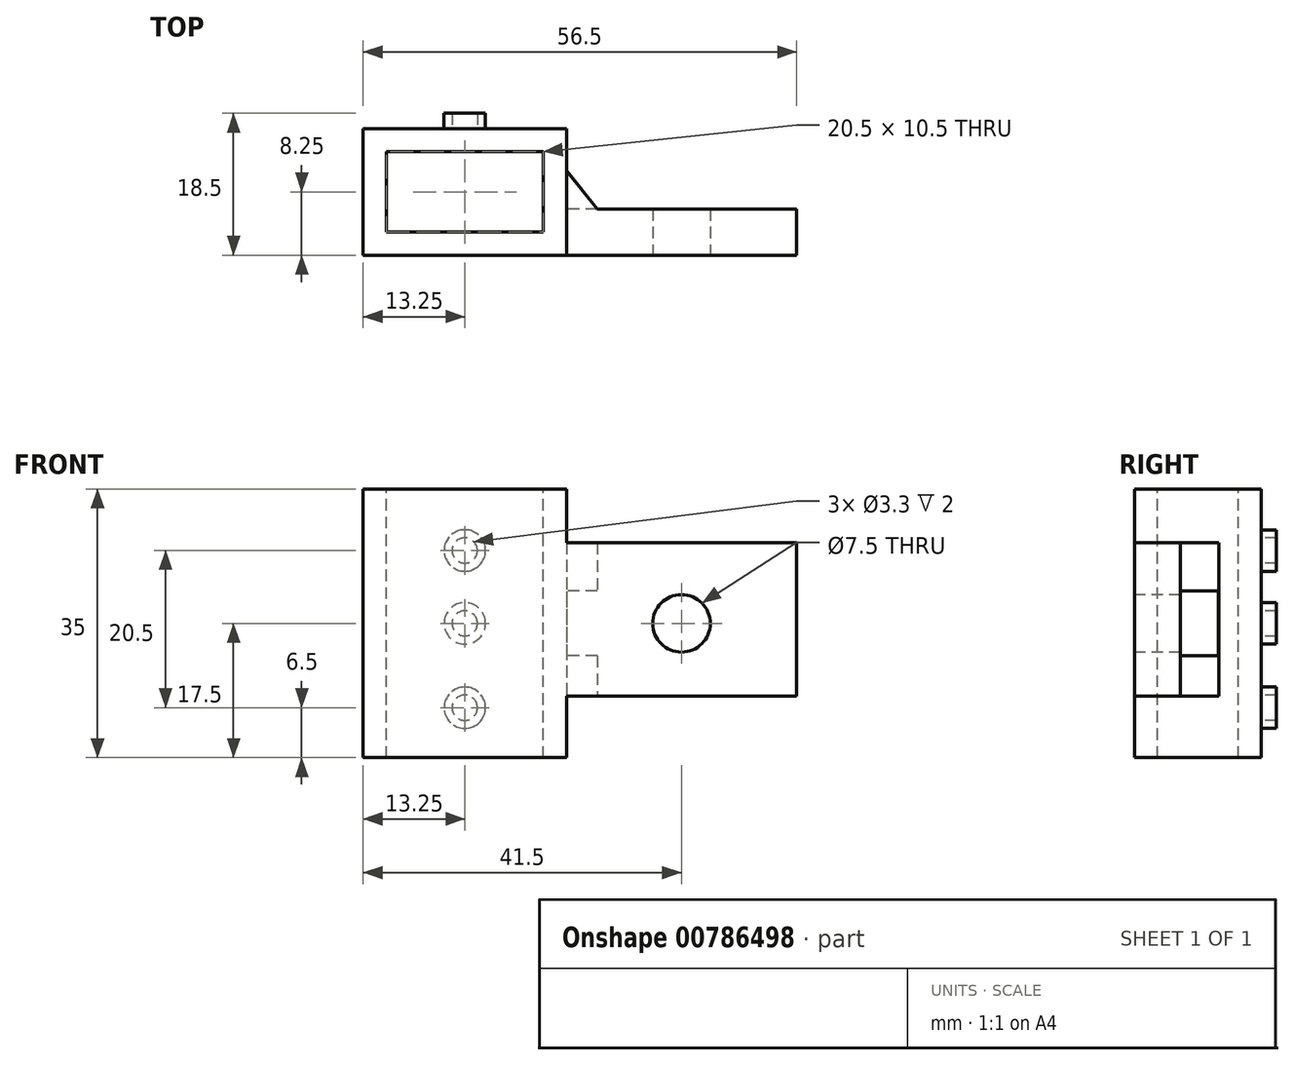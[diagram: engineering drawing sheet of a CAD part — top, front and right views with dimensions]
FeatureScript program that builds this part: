
annotation { "Feature Type Name" : "Feature", "Feature Type Description" : "" }
export const myFeature = defineFeature(function(context is Context, id is Id, definition is map)
    precondition{}
    {
        {
            var Q0;
            Q0=qCreatedBy(makeId("Front.planeOp"),FACE);
            var sketch = newSketch(context, id + "F0", { "sketchPlane" : qUnion([Q0])});
            skLineSegment(sketch, "E0.bottom", {"start": v(-13.25, 17.5) * mm, "end": v(13.25, 17.5) * mm});
            skLineSegment(sketch, "E0.top", {"start": v(-13.25, -17.5) * mm, "end": v(13.25, -17.5) * mm});
            skLineSegment(sketch, "E0.left", {"start": v(-13.25, 17.5) * mm, "end": v(-13.25, -17.5) * mm});
            skLineSegment(sketch, "E0.right", {"start": v(13.25, 17.5) * mm, "end": v(13.25, -17.5) * mm});
            skSolve(sketch);
        }
        {
            var Q0;
            Q0 = qSketchRegion(id + "F0", true);
            extrude(context, id + "F1", {"entities" : qUnion([Q0]), "depth" : 16.5 * mm, "offsetDistance" : 25 * mm});
        }
        {
            var Q0;
            Q0=makeQuery(id+"F1.opExtrude","SWEPT_FACE",FACE,{"disambiguationData":[OSD([sQuery(id+"F0.wireOp",EDGE,"E0.bottom")])]});
            var sketch = newSketch(context, id + "F2", { "sketchPlane" : qUnion([Q0])});
            skLineSegment(sketch, "E1.bottom", {"start": v(-10.25, -3) * mm, "end": v(10.25, -3) * mm});
            skLineSegment(sketch, "E1.top", {"start": v(-10.25, -13.5) * mm, "end": v(10.25, -13.5) * mm});
            skLineSegment(sketch, "E1.left", {"start": v(-10.25, -3) * mm, "end": v(-10.25, -13.5) * mm});
            skLineSegment(sketch, "E1.right", {"start": v(10.25, -3) * mm, "end": v(10.25, -13.5) * mm});
            skSolve(sketch);
        }
        {
            var Q0;
            Q0 = qSketchRegion(id + "F2", true);
            extrude(context, id + "F3", {"entities" : qUnion([Q0]), "operationType" : NewBodyOperationType.REMOVE, "oppositeDirection" : true, "depth" : 35 * mm, "offsetDistance" : 25 * mm});
        }
        {
            var Q0;
            Q0=makeQuery(id+"F1.opExtrude","SWEPT_FACE",FACE,{"disambiguationData":[OSD([sQuery(id+"F0.wireOp",EDGE,"E0.right")])]});
            var sketch = newSketch(context, id + "F4", { "sketchPlane" : qUnion([Q0])});
            skLineSegment(sketch, "E2.bottom", {"start": v(-16.5, 10.5) * mm, "end": v(-10.5, 10.5) * mm});
            skLineSegment(sketch, "E2.top", {"start": v(-16.5, -9.5) * mm, "end": v(-10.5, -9.5) * mm});
            skLineSegment(sketch, "E2.left", {"start": v(-16.5, 10.5) * mm, "end": v(-16.5, -9.5) * mm});
            skLineSegment(sketch, "E2.right", {"start": v(-10.5, 10.5) * mm, "end": v(-10.5, -9.5) * mm});
            skSolve(sketch);
        }
        {
            var Q0;
            Q0 = qSketchRegion(id + "F4", true);
            extrude(context, id + "F5", {"entities" : qUnion([Q0]), "operationType" : NewBodyOperationType.ADD, "depth" : 30 * mm, "offsetDistance" : 25 * mm});
        }
        {
            var Q0;
            Q0=makeQuery(id+"F5.opExtrude","SWEPT_FACE",FACE,{"disambiguationData":[OSD([sQuery(id+"F4.wireOp",EDGE,"E2.top")])]});
            var sketch = newSketch(context, id + "F6", { "sketchPlane" : qUnion([Q0])});
            skLineSegment(sketch, "E3", {"start": v(17.25, 10.5) * mm, "end": v(13.25, 5.5) * mm});
            skLineSegment(sketch, "E4", {"start": v(17.25, 10.5) * mm, "end": v(13.25, 10.5) * mm});
            skLineSegment(sketch, "E5", {"start": v(13.25, 10.5) * mm, "end": v(13.25, 5.5) * mm});
            skSolve(sketch);
        }
        {
            var Q0;
            Q0 = qSketchRegion(id + "F6", true);
            extrude(context, id + "F7", {"entities" : qUnion([Q0]), "operationType" : NewBodyOperationType.ADD, "oppositeDirection" : true, "depth" : 20 * mm, "offsetDistance" : 25 * mm});
        }
        {
            var Q0;
            Q0=makeQuery(id+"F5.boolean.opBoolean","MERGE",FACE,{"derivedFrom":[makeQuery(id+"F1.opExtrude","CAP_FACE",FACE,{"disambiguationData":[OSD([sQuery(id+"F0.wireOp",EDGE,"E0.bottom"),sQuery(id+"F0.wireOp",EDGE,"E0.top"),sQuery(id+"F0.wireOp",EDGE,"E0.left"),sQuery(id+"F0.wireOp",EDGE,"E0.right")])],"isStart":false}),makeQuery(id+"F5.opExtrude","SWEPT_FACE",FACE,{"disambiguationData":[OSD([sQuery(id+"F4.wireOp",EDGE,"E2.left")])]})]});
            var sketch = newSketch(context, id + "F8", { "sketchPlane" : qUnion([Q0])});
            skCircle(sketch, "E6", {"center": v(28.25, 0) * mm, "radius": 3.75 * mm});
            skSolve(sketch);
        }
        {
            var Q0;
            Q0 = qSketchRegion(id + "F8", true);
            extrude(context, id + "F9", {"entities" : qUnion([Q0]), "operationType" : NewBodyOperationType.REMOVE, "oppositeDirection" : true, "depth" : 25 * mm, "offsetDistance" : 25 * mm});
        }
        {
            var Q0;
            Q0=makeQuery(id+"F5.opExtrude","SWEPT_FACE",FACE,{"disambiguationData":[OSD([sQuery(id+"F4.wireOp",EDGE,"E2.right")])]});
            var sketch = newSketch(context, id + "F10", { "sketchPlane" : qUnion([Q0])});
            skLineSegment(sketch, "E7.bottom", {"start": v(-17.25, -4.24) * mm, "end": v(-13.3, -4.24) * mm});
            skLineSegment(sketch, "E7.top", {"start": v(-17.25, 4.26) * mm, "end": v(-13.3, 4.26) * mm});
            skLineSegment(sketch, "E7.left", {"start": v(-17.25, -4.25) * mm, "end": v(-17.25, 4.26) * mm});
            skLineSegment(sketch, "E7.right", {"start": v(-13.3, -4.24) * mm, "end": v(-13.3, 4.26) * mm});
            skSolve(sketch);
        }
        {
            var Q0;
            Q0 = qSketchRegion(id + "F10", true);
            extrude(context, id + "F11", {"entities" : qUnion([Q0]), "operationType" : NewBodyOperationType.REMOVE, "depth" : 25 * mm, "offsetDistance" : 25 * mm});
        }
        {
            var Q0;
            Q0=makeQuery(id+"F1.opExtrude","CAP_FACE",FACE,{"disambiguationData":[OSD([sQuery(id+"F0.wireOp",EDGE,"E0.bottom"),sQuery(id+"F0.wireOp",EDGE,"E0.top"),sQuery(id+"F0.wireOp",EDGE,"E0.left"),sQuery(id+"F0.wireOp",EDGE,"E0.right")])],"isStart":true});
            var sketch = newSketch(context, id + "F12", { "sketchPlane" : qUnion([Q0])});
            skCircle(sketch, "E8", {"center": v(0, 0) * mm, "radius": 1.65 * mm});
            skCircle(sketch, "E9", {"center": v(0, 0) * mm, "radius": 2.7 * mm});
            skCircle(sketch, "E10.MirrorC", {"center": v(0, 9.5) * mm, "radius": 1.65 * mm});
            skCircle(sketch, "E11.MirrorC", {"center": v(0, 9.5) * mm, "radius": 2.7 * mm});
            skCircle(sketch, "E12.MirrorC", {"center": v(0, -11) * mm, "radius": 1.65 * mm});
            skCircle(sketch, "E13.MirrorC", {"center": v(0, -11) * mm, "radius": 2.7 * mm});
            skSolve(sketch);
        }
        {
            var Q0;
            Q0 = qSketchRegion(id + "F12", true);
            extrude(context, id + "F13", {"entities" : qUnion([Q0]), "operationType" : NewBodyOperationType.ADD, "depth" : 2 * mm, "offsetDistance" : 25 * mm});
        }
    });
